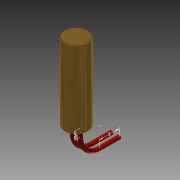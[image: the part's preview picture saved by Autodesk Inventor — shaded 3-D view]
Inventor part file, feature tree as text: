
AUTODESK INVENTOR PART (.ipt)
format: ipt  version: 2015 (Build 190159000, 159)  size: 148,480 bytes
history: native  units: mm
features: sketch x5, other x3, extrude x2, sweep x2, fillet x1
ambient origin geometry x8: Origin, YZ Plane, XZ Plane, XY Plane, X Axis, Y Axis, Z Axis, Center Point
bodies: Body1 (feature_tree)
feature tree (13):
  other  "Твердое тело1"
  extrude  "Выдавливание1"  Depth=6.0mm
  fillet  "Сопряжение1"  Radius=20.0mm
  extrude  "Выдавливание2"  Depth=0.5mm
  other  "РабПлоскость1"
  sketch  "Эскиз3"
  sketch  "Эскиз4"
  sweep  "Сдвиг1"
  other  "РабПлоскость2"
  sweep  "Сдвиг2"
  sketch  "Эскиз1"
  sketch  "Эскиз2"
  sketch  "Эскиз5"
